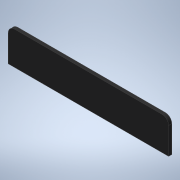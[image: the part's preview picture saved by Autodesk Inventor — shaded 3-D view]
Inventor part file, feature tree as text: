
AUTODESK INVENTOR PART (.ipt)
format: ipt  version: 2020 (Build 240168000, 168)  size: 103,424 bytes
history: native  units: mm
features: other x1, extrude x1, fillet x1
ambient origin geometry x8: Origin, YZ Plane, XZ Plane, XY Plane, X Axis, Y Axis, Z Axis, Center Point
bodies: Body1 (feature_tree)
feature tree (3):
  other  "實體1"
  extrude  "擠出1"  Depth=26.0mm
  fillet  "圓角1"  Radius=126.0mm
